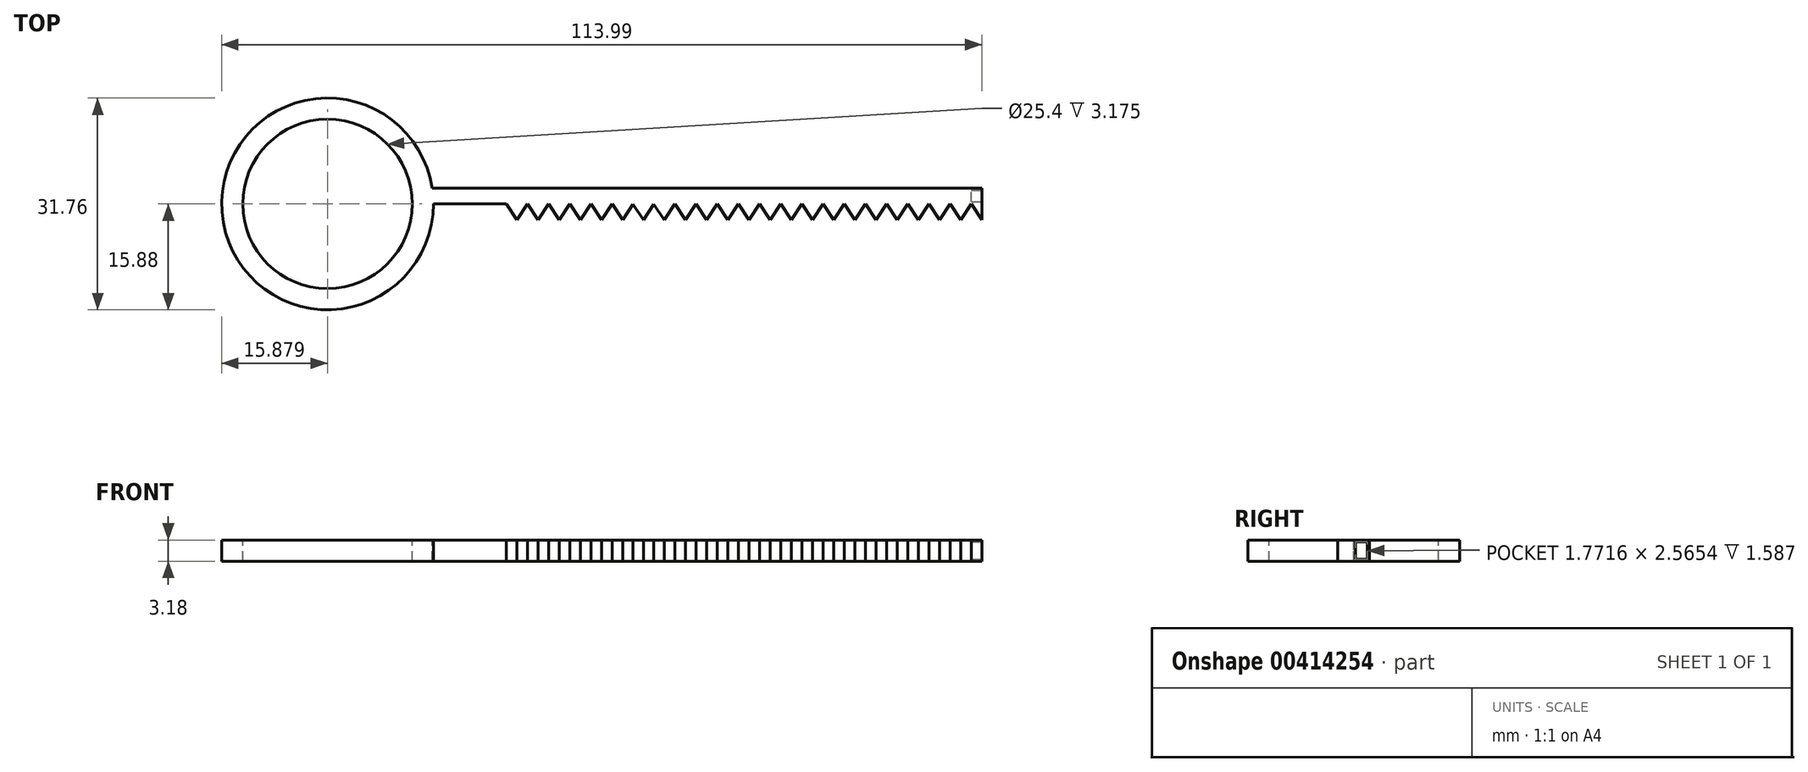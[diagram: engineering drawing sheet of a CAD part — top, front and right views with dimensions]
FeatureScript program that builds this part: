
annotation { "Feature Type Name" : "Feature", "Feature Type Description" : "" }
export const myFeature = defineFeature(function(context is Context, id is Id, definition is map)
    precondition{}
    {
        {
            var Q0;
            Q0=qCreatedBy(makeId("Front.planeOp"),FACE);
            var sketch = newSketch(context, id + "F0", { "sketchPlane" : qUnion([Q0])});
            skLineSegment(sketch, "E0.bottom", {"start": v(-63.26, 3.18) * mm, "end": v(-60.08, 3.18) * mm});
            skLineSegment(sketch, "E0.top", {"start": v(-63.26, 0) * mm, "end": v(-60.08, 0) * mm});
            skLineSegment(sketch, "E0.left", {"start": v(-63.26, 3.18) * mm, "end": v(-63.26, 0) * mm});
            skLineSegment(sketch, "E0.right", {"start": v(-60.08, 3.18) * mm, "end": v(-60.08, 0) * mm});
            skLineSegment(sketch, "E1", {"start": v(-60.08, 3.17) * mm, "end": v(-47.38, 3.18) * mm});
            skLineSegment(sketch, "E2", {"start": v(-47.38, 3.18) * mm, "end": v(-47.38, 0) * mm});
            skSolve(sketch);
        }
        {
            var Q0;
            Q0=makeQuery(id+"F0.imprint","IMPRINT",FACE,{"disambiguationData":[TD([[makeQuery(id+"F0.imprint","IMPRINT",EDGE,{"derivedFrom":sQuery(id+"F0.wireOp",EDGE,"E0.bottom")}),-1.0]])]});
            var Q1;
            Q1=sQuery(id+"F0.wireOp",EDGE,"E2");
            revolve(context, id + "F1", {"entities" : qUnion([Q0]), "axis" : qUnion([Q1]), "revolveType" : RevolveType.FULL});
        }
        {
            var Q0;
            Q0=qCreatedBy(makeId("Top.planeOp"),FACE);
            var sketch = newSketch(context, id + "F2", { "sketchPlane" : qUnion([Q0])});
            skLineSegment(sketch, "E3", {"start": v(-31.82, 0) * mm, "end": v(-31.82, 2.38) * mm});
            skLineSegment(sketch, "E4", {"start": v(-31.82, 0) * mm, "end": v(-31.82, -2.38) * mm});
            skLineSegment(sketch, "E5", {"start": v(-31.82, 2.38) * mm, "end": v(50.73, 2.38) * mm});
            skLineSegment(sketch, "E6", {"start": v(-31.82, -2.38) * mm, "end": v(50.73, -2.38) * mm});
            skLineSegment(sketch, "E7", {"start": v(50.73, -2.38) * mm, "end": v(47.56, -2.38) * mm});
            skLineSegment(sketch, "E8", {"start": v(50.73, 2.38) * mm, "end": v(50.73, -2.38) * mm});
            skPoint(sketch, "E9.endSnap0", {"position": v(49.14, -2.38) * mm});
            skLineSegment(sketch, "E10", {"start": v(-33.54, -7.8) * mm, "end": v(-31.82, -2.38) * mm});
            skLineSegment(sketch, "E11", {"start": v(47.56, -2.38) * mm, "end": v(49.14, 0) * mm});
            skLineSegment(sketch, "E12", {"start": v(49.14, 0) * mm, "end": v(50.73, -2.38) * mm});
            skLineSegment(sketch, "E13.MirrorCS", {"start": v(47.56, -2.38) * mm, "end": v(45.97, 0) * mm});
            skLineSegment(sketch, "E14.MirrorCS", {"start": v(45.97, 0) * mm, "end": v(44.38, -2.38) * mm});
            skLineSegment(sketch, "E15.MirrorCS", {"start": v(42.8, 0) * mm, "end": v(44.38, -2.38) * mm});
            skLineSegment(sketch, "E16.MirrorCS", {"start": v(41.2, -2.38) * mm, "end": v(42.8, 0) * mm});
            skLineSegment(sketch, "E17.MirrorCS", {"start": v(41.2, -2.38) * mm, "end": v(39.62, 0) * mm});
            skLineSegment(sketch, "E18.MirrorCS", {"start": v(39.62, 0) * mm, "end": v(38.03, -2.38) * mm});
            skLineSegment(sketch, "E19.MirrorCS", {"start": v(36.44, 0) * mm, "end": v(38.03, -2.38) * mm});
            skLineSegment(sketch, "E20.MirrorCS", {"start": v(34.86, -2.38) * mm, "end": v(36.44, 0) * mm});
            skLineSegment(sketch, "E21.MirrorCS", {"start": v(34.86, -2.38) * mm, "end": v(33.27, 0) * mm});
            skLineSegment(sketch, "E22.MirrorCS", {"start": v(33.27, 0) * mm, "end": v(31.68, -2.38) * mm});
            skLineSegment(sketch, "E23.MirrorCS", {"start": v(30.1, 0) * mm, "end": v(31.68, -2.38) * mm});
            skLineSegment(sketch, "E24.MirrorCS", {"start": v(28.5, -2.38) * mm, "end": v(30.1, 0) * mm});
            skLineSegment(sketch, "E25.MirrorCS", {"start": v(28.5, -2.38) * mm, "end": v(26.92, 0) * mm});
            skLineSegment(sketch, "E26.MirrorCS", {"start": v(26.92, 0) * mm, "end": v(25.33, -2.38) * mm});
            skLineSegment(sketch, "E27.MirrorCS", {"start": v(23.74, 0) * mm, "end": v(25.33, -2.38) * mm});
            skLineSegment(sketch, "E28.MirrorCS", {"start": v(22.16, -2.38) * mm, "end": v(23.74, 0) * mm});
            skLineSegment(sketch, "E29.MirrorCS", {"start": v(22.16, -2.38) * mm, "end": v(20.57, 0) * mm});
            skLineSegment(sketch, "E30.MirrorCS", {"start": v(20.57, 0) * mm, "end": v(18.98, -2.38) * mm});
            skLineSegment(sketch, "E31.MirrorCS", {"start": v(17.4, 0) * mm, "end": v(18.98, -2.38) * mm});
            skLineSegment(sketch, "E32.MirrorCS", {"start": v(15.8, -2.38) * mm, "end": v(17.4, 0) * mm});
            skLineSegment(sketch, "E33.MirrorCS", {"start": v(15.8, -2.38) * mm, "end": v(14.22, 0) * mm});
            skLineSegment(sketch, "E34.MirrorCS", {"start": v(14.22, 0) * mm, "end": v(12.63, -2.38) * mm});
            skLineSegment(sketch, "E35.MirrorCS", {"start": v(11.04, 0) * mm, "end": v(12.63, -2.38) * mm});
            skLineSegment(sketch, "E36.MirrorCS", {"start": v(9.46, -2.38) * mm, "end": v(11.04, 0) * mm});
            skLineSegment(sketch, "E37.MirrorCS", {"start": v(9.46, -2.38) * mm, "end": v(7.87, 0) * mm});
            skLineSegment(sketch, "E38.MirrorCS", {"start": v(7.87, 0) * mm, "end": v(6.28, -2.38) * mm});
            skLineSegment(sketch, "E39.MirrorCS", {"start": v(4.7, 0) * mm, "end": v(6.28, -2.38) * mm});
            skLineSegment(sketch, "E40.MirrorCS", {"start": v(3.1, -2.38) * mm, "end": v(4.7, 0) * mm});
            skLineSegment(sketch, "E41.MirrorCS", {"start": v(3.1, -2.38) * mm, "end": v(1.52, 0) * mm});
            skLineSegment(sketch, "E42.MirrorCS", {"start": v(1.59, 0) * mm, "end": v(0, -2.38) * mm});
            skLineSegment(sketch, "E43.MirrorCS", {"start": v(-1.59, 0) * mm, "end": v(0, -2.38) * mm});
            skLineSegment(sketch, "E44.MirrorCS", {"start": v(-3.1, -2.38) * mm, "end": v(-1.52, 0) * mm});
            skLineSegment(sketch, "E45.MirrorCS", {"start": v(-3.1, -2.38) * mm, "end": v(-4.7, 0) * mm});
            skLineSegment(sketch, "E46.MirrorCS", {"start": v(-4.7, 0) * mm, "end": v(-6.28, -2.38) * mm});
            skLineSegment(sketch, "E47.MirrorCS", {"start": v(-7.87, 0) * mm, "end": v(-6.28, -2.38) * mm});
            skLineSegment(sketch, "E48.MirrorCS", {"start": v(-9.46, -2.38) * mm, "end": v(-7.87, 0) * mm});
            skLineSegment(sketch, "E49.MirrorCS", {"start": v(-9.46, -2.38) * mm, "end": v(-11.04, 0) * mm});
            skLineSegment(sketch, "E50.MirrorCS", {"start": v(-11.04, 0) * mm, "end": v(-12.63, -2.38) * mm});
            skLineSegment(sketch, "E51.MirrorCS", {"start": v(-14.22, 0) * mm, "end": v(-12.63, -2.38) * mm});
            skLineSegment(sketch, "E52.MirrorCS", {"start": v(-15.8, -2.38) * mm, "end": v(-14.22, 0) * mm});
            skLineSegment(sketch, "E53.MirrorCS", {"start": v(-15.8, -2.38) * mm, "end": v(-17.4, 0) * mm});
            skLineSegment(sketch, "E54.MirrorCS", {"start": v(-17.4, 0) * mm, "end": v(-18.98, -2.38) * mm});
            skLineSegment(sketch, "E55.MirrorCS", {"start": v(-20.57, 0) * mm, "end": v(-18.98, -2.38) * mm});
            skLineSegment(sketch, "E56.MirrorCS", {"start": v(-22.16, -2.38) * mm, "end": v(-20.57, 0) * mm});
            skLineSegment(sketch, "E57", {"start": v(-20.57, 0) * mm, "end": v(-31.82, 0) * mm});
            skSolve(sketch);
        }
        {
            var Q0;
            {var subQ4=sQuery(id+"F2.wireOp",EDGE,"OUriN0MP-dP0G-YcSs-nnOM-vSAOMxgyIstP");Q0=makeQuery(id+"F2.imprint","IMPRINT",FACE,{"disambiguationData":[TD([[makeQuery(id+"F2.imprint","IMPRINT",EDGE,{"derivedFrom":subQ4}),1.0]])]});}
            var Q1;
            Q1=makeQuery(id+"F2.imprint","IMPRINT",FACE,{"disambiguationData":[TD([[makeQuery(id+"F2.imprint","IMPRINT",EDGE,{"derivedFrom":sQuery(id+"F2.wireOp",EDGE,"E3")}),-1.0]])]});
            extrude(context, id + "F3", {"entities" : qUnion([Q0, Q1]), "operationType" : NewBodyOperationType.ADD, "depth" : 3.17 * mm});
        }
        {
            var Q0;
            Q0=makeQuery(id+"F3.opExtrude","SWEPT_FACE",FACE,{"disambiguationData":[OSD([sQuery(id+"F2.wireOp",EDGE,"E8")])]});
            var sketch = newSketch(context, id + "F4", { "sketchPlane" : qUnion([Q0])});
            skLineSegment(sketch, "E58", {"start": v(0, 3.18) * mm, "end": v(2.38, 3.18) * mm});
            skLineSegment(sketch, "E59", {"start": v(0, 0) * mm, "end": v(0.3, 0) * mm});
            skLineSegment(sketch, "E60", {"start": v(0.3, 0) * mm, "end": v(0.3, 0.3) * mm});
            skLineSegment(sketch, "E61.MirrorCS", {"start": v(2.08, 0) * mm, "end": v(2.08, 0.3) * mm});
            skLineSegment(sketch, "E62.MirrorCS", {"start": v(2.38, 0) * mm, "end": v(2.08, 0) * mm});
            skLineSegment(sketch, "E63.MirrorCS", {"start": v(2.08, 3.18) * mm, "end": v(2.08, 2.87) * mm});
            skLineSegment(sketch, "E64.MirrorCS", {"start": v(2.38, 3.18) * mm, "end": v(2.08, 3.18) * mm});
            skLineSegment(sketch, "E65.MirrorCS", {"start": v(0.3, 3.18) * mm, "end": v(0.3, 2.87) * mm});
            skLineSegment(sketch, "E66.MirrorCS", {"start": v(0, 3.18) * mm, "end": v(0.3, 3.18) * mm});
            skLineSegment(sketch, "E67.bottom", {"start": v(0.3, 2.87) * mm, "end": v(2.08, 2.87) * mm});
            skLineSegment(sketch, "E67.top", {"start": v(0.3, 0.3) * mm, "end": v(2.08, 0.3) * mm});
            skLineSegment(sketch, "E67.left", {"start": v(0.3, 2.87) * mm, "end": v(0.3, 0.3) * mm});
            skLineSegment(sketch, "E67.right", {"start": v(2.08, 2.87) * mm, "end": v(2.08, 0.3) * mm});
            skSolve(sketch);
        }
        {
            var Q0;
            Q0=makeQuery(id+"F4.imprint","IMPRINT",FACE,{"disambiguationData":[TD([[makeQuery(id+"F4.imprint","IMPRINT",EDGE,{"derivedFrom":sQuery(id+"F4.wireOp",EDGE,"E67.bottom")}),-1.0]])]});
            extrude(context, id + "F5", {"entities" : qUnion([Q0]), "operationType" : NewBodyOperationType.REMOVE, "oppositeDirection" : true, "depth" : 1.59 * mm});
        }
    });
